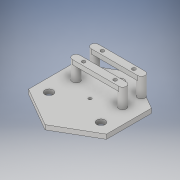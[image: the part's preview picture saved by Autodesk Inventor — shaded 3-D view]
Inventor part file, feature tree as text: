
AUTODESK INVENTOR PART (.ipt)
format: ipt  version: 2019 (Build 230136000, 136)  size: 191,488 bytes
history: native  units: mm
features: extrude x6, sketch x6
ambient origin geometry x8: Origin, YZ Plane, XZ Plane, XY Plane, X Axis, Y Axis, Z Axis, Center Point
bodies: Solid1 (feature_tree)
feature tree (12):
  extrude  "Extrusion1"  TaperAngle=150.0deg  [1 undecoded]
  extrude  "Extrusion2"  TaperAngle=90.0deg  [1 undecoded]
  extrude  "Extrusion4"  TaperAngle=120.0deg  [1 undecoded]
  extrude  "Extrusion5"  Depth=3.0mm TaperAngle=0.0deg
  extrude  "Extrusion6"  Depth=5.5mm
  extrude  "Extrusion7"  TaperAngle=30.0deg  [1 undecoded]
  sketch  "Sketch1"  dims[d0=30.0mm d1=150.0deg]
  sketch  "Sketch2"  dims[d3=30.0mm d4=90.0deg]
  sketch  "Sketch3"  dims[d5=30.0mm d6=120.0deg]
  sketch  "Sketch4"  dims[d7=25.980762mm d8=3.0mm d9=0.0mm]
  sketch  "Sketch5"  dims[d10=20.0mm d11=5.5mm]
  sketch  "Sketch6"  dims[d12=20.0mm d13=30.0deg d14=20.0mm d15=150.0deg d16=5.5mm d17=5.5mm d18=10.0mm d19=0.0mm d20=12.5mm d21=21.0mm d22=12.5mm d29=5.0mm d30=5.0mm d31=5.0mm d32=0.0mm d33=5.0mm d34=5.0mm d35=5.0mm d36=5.0mm d37=5.0mm d38=10.0mm d39=0.0mm d40=31.0mm d41=5.0mm d42=2.5mm d43=31.0mm d44=5.0mm d49=2.5mm d50=3.0mm d51=0.0mm d52=5.0mm d53=5.0mm d54=5.0mm d55=5.0mm d56=2.3mm d57=2.3mm d58=2.3mm d59=2.3mm d60=3.0mm d61=0.0mm d62=2.0mm d63=10.0mm d64=0.0mm]
note: 4 required parameter values undecoded (feature->parameter linkage not recoverable at this tier; creation-order binding heuristic only, values carry confidence <= 0.55)
